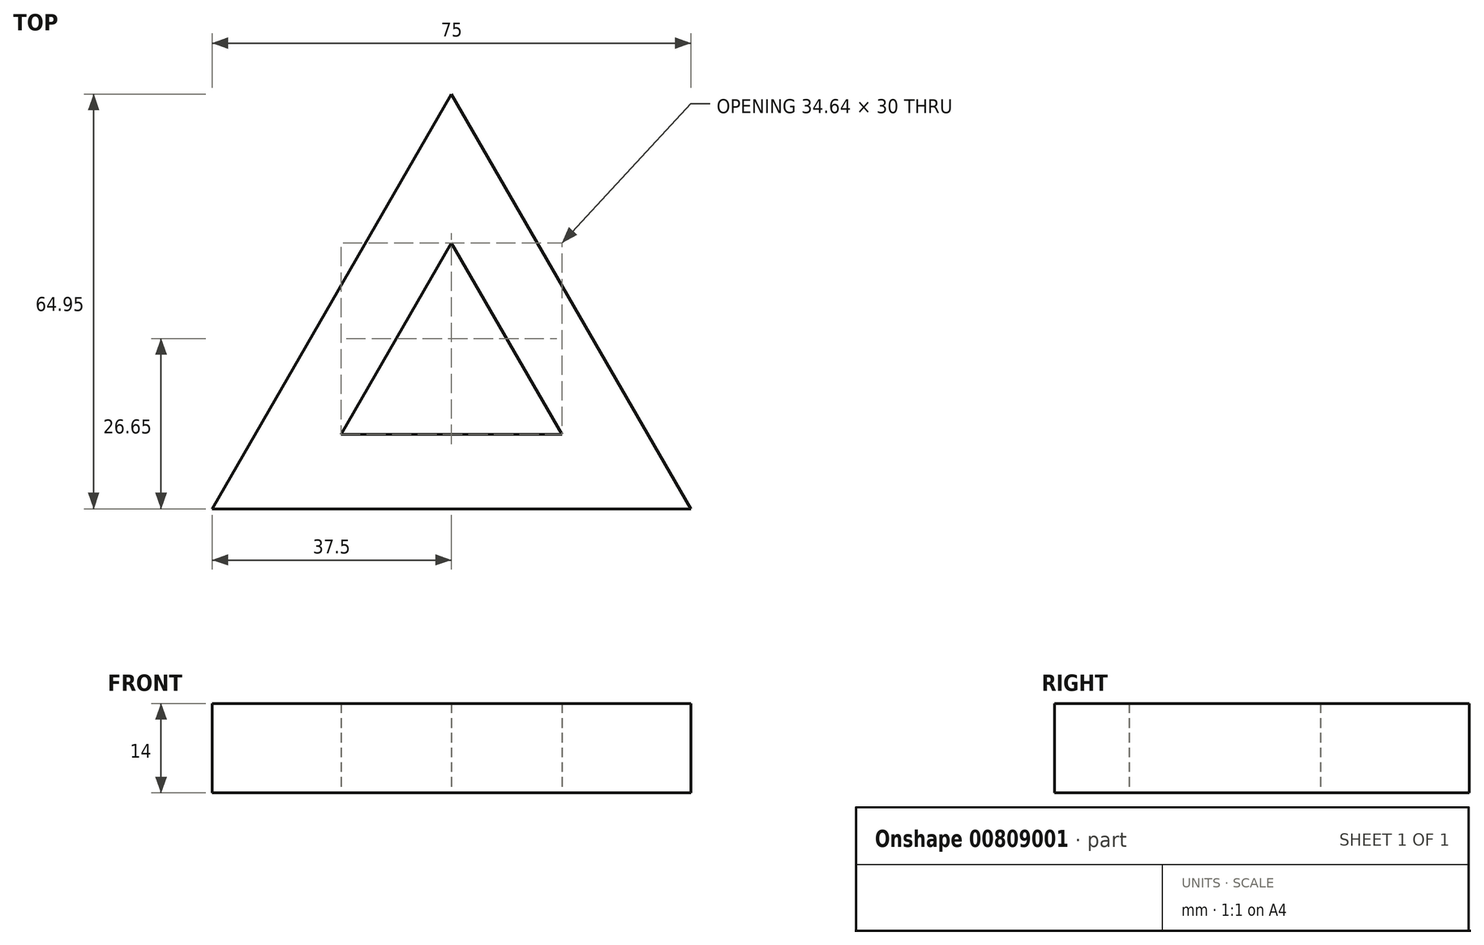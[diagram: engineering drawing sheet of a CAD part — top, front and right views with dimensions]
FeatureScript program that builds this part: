
annotation { "Feature Type Name" : "Feature", "Feature Type Description" : "" }
export const myFeature = defineFeature(function(context is Context, id is Id, definition is map)
    precondition{}
    {
        {
            var Q0;
            Q0=qCreatedBy(makeId("Top.planeOp"),FACE);
            var sketch = newSketch(context, id + "F0", { "sketchPlane" : qUnion([Q0])});
            skCircle(sketch, "E0.cCircle", {"center": v(0, 0) * mm, "radius": 21.65 * mm, "construction": true});
            skLineSegment(sketch, "E0.0", {"start": v(-37.5, -21.65) * mm, "end": v(0, 43.3) * mm});
            skLineSegment(sketch, "E0.1", {"start": v(0, 43.3) * mm, "end": v(37.5, -21.65) * mm});
            skLineSegment(sketch, "E0.2", {"start": v(37.5, -21.65) * mm, "end": v(-37.5, -21.65) * mm});
            skPoint(sketch, "E0.0.midPoint", {"position": v(-18.75, 10.83) * mm});
            skCircle(sketch, "E1.cCircle", {"center": v(0, 0) * mm, "radius": 10 * mm, "construction": true});
            skLineSegment(sketch, "E1.0", {"start": v(17.32, -10) * mm, "end": v(-17.32, -10) * mm});
            skLineSegment(sketch, "E1.1", {"start": v(-17.32, -10) * mm, "end": v(0, 20) * mm});
            skLineSegment(sketch, "E1.2", {"start": v(0, 20) * mm, "end": v(17.32, -10) * mm});
            skPoint(sketch, "E1.0.midPoint", {"position": v(0, -10) * mm});
            skLineSegment(sketch, "E2", {"start": v(-37.5, -21.65) * mm, "end": v(-17.32, -10) * mm, "construction": true});
            skLineSegment(sketch, "E3", {"start": v(0, 20) * mm, "end": v(0, 43.3) * mm, "construction": true});
            skLineSegment(sketch, "E4", {"start": v(17.32, -10) * mm, "end": v(37.5, -21.65) * mm, "construction": true});
            skPoint(sketch, "E5", {"position": v(8.66, 5) * mm});
            skPoint(sketch, "E6", {"position": v(18.75, 10.83) * mm});
            skSolve(sketch);
        }
        {
            var Q0;
            Q0=makeQuery(id+"F0.imprint","IMPRINT",FACE,{"disambiguationData":[TD([[makeQuery(id+"F0.imprint","IMPRINT",EDGE,{"derivedFrom":sQuery(id+"F0.wireOp",EDGE,"E0.0")}),-1.0]])]});
            extrude(context, id + "F1", {"entities" : qUnion([Q0]), "endBound" : BoundingType.SYMMETRIC, "depth" : 14 * mm, "offsetDistance" : 25 * mm});
        }
    });
